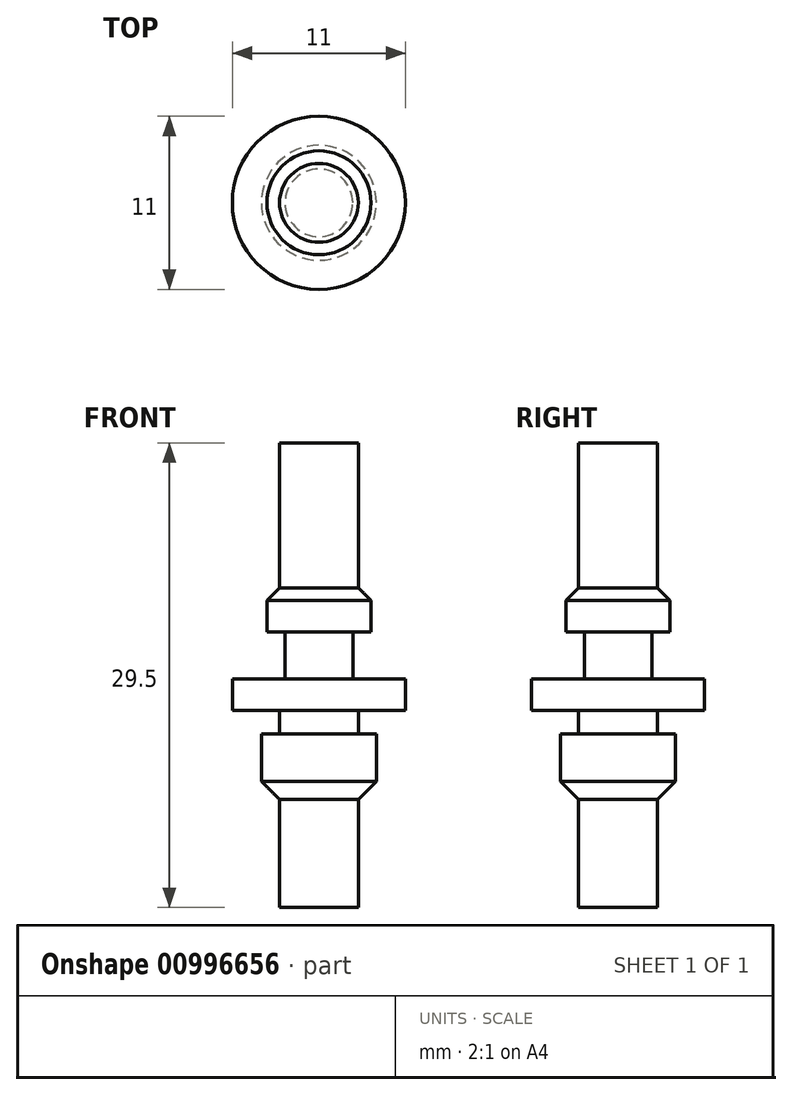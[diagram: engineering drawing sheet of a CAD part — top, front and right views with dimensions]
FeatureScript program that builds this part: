
annotation { "Feature Type Name" : "Feature", "Feature Type Description" : "" }
export const myFeature = defineFeature(function(context is Context, id is Id, definition is map)
    precondition{}
    {
        {
            var Q0;
            Q0=qCreatedBy(makeId("Top.planeOp"),FACE);
            var sketch = newSketch(context, id + "F0", { "sketchPlane" : qUnion([Q0])});
            skCircle(sketch, "E0", {"center": v(0, 0) * mm, "radius": 5.5 * mm});
            skSolve(sketch);
        }
        {
            var Q0;
            Q0=qSketchRegion(id+"F0",true);
            extrude(context, id + "F1", {"entities" : qUnion([Q0]), "depth" : 2 * mm, "offsetDistance" : 25 * mm});
        }
        {
            var Q0;
            Q0=makeQuery(id+"F1.opExtrude","CAP_FACE",FACE,{"disambiguationData":[OSD([sQuery(id+"F0.wireOp",EDGE,"E0")])],"isStart":false});
            var sketch = newSketch(context, id + "F2", { "sketchPlane" : qUnion([Q0])});
            skCircle(sketch, "E1", {"center": v(0, 0) * mm, "radius": 2.15 * mm});
            skSolve(sketch);
        }
        {
            var Q0;
            Q0=qSketchRegion(id+"F2",true);
            extrude(context, id + "F3", {"entities" : qUnion([Q0]), "operationType" : NewBodyOperationType.ADD, "depth" : 3 * mm, "offsetDistance" : 25 * mm});
        }
        {
            var Q0;
            Q0=makeQuery(id+"F3.opExtrude","CAP_FACE",FACE,{"disambiguationData":[OSD([sQuery(id+"F2.wireOp",EDGE,"E1")])],"isStart":false});
            var sketch = newSketch(context, id + "F4", { "sketchPlane" : qUnion([Q0])});
            skCircle(sketch, "E2", {"center": v(0, 0) * mm, "radius": 3.3 * mm});
            skSolve(sketch);
        }
        {
            var Q0;
            Q0=qSketchRegion(id+"F4",true);
            extrude(context, id + "F5", {"entities" : qUnion([Q0]), "operationType" : NewBodyOperationType.ADD, "depth" : 12 * mm, "offsetDistance" : 25 * mm});
        }
        {
            var Q0;
            Q0=makeQuery(id+"F5.opExtrude","CAP_FACE",FACE,{"disambiguationData":[OSD([sQuery(id+"F4.wireOp",EDGE,"E2")])],"isStart":false});
            var sketch = newSketch(context, id + "F6", { "sketchPlane" : qUnion([Q0])});
            skCircle(sketch, "E3", {"center": v(0, 0) * mm, "radius": 2.5 * mm});
            skCircle(sketch, "E4", {"center": v(0, 0) * mm, "radius": 5 * mm});
            skSolve(sketch);
        }
        {
            var Q0;
            Q0=qSketchRegion(id+"F6",true);
            extrude(context, id + "F7", {"entities" : qUnion([Q0]), "operationType" : NewBodyOperationType.REMOVE, "oppositeDirection" : true, "depth" : 7 * mm, "offsetDistance" : 25 * mm});
        }
        {
            var Q0;
            Q0=makeQuery(id+"F7.boolean.opBoolean","INTERSECT",EDGE,{"derivedFrom":[makeQuery(id+"F5.opExtrude","SWEPT_FACE",FACE,{"disambiguationData":[OSD([sQuery(id+"F4.wireOp",EDGE,"E2")])]}),makeQuery(id+"F7.opExtrude","CAP_FACE",FACE,{"disambiguationData":[OSD([sQuery(id+"F6.wireOp",EDGE,"E3"),sQuery(id+"F6.wireOp",EDGE,"E4")])],"isStart":false})]});
            chamfer(context, id + "F8", {"entities" : qUnion([Q0]), "width" : 3 * mm, "tangentPropagation" : true});
        }
        {
            var Q0;
            Q0=makeQuery(id+"F1.opExtrude","CAP_FACE",FACE,{"disambiguationData":[OSD([sQuery(id+"F0.wireOp",EDGE,"E0")])],"isStart":true});
            var sketch = newSketch(context, id + "F9", { "sketchPlane" : qUnion([Q0])});
            skCircle(sketch, "E5", {"center": v(0, 0) * mm, "radius": 2.5 * mm});
            skSolve(sketch);
        }
        {
            var Q0;
            Q0=qSketchRegion(id+"F9",true);
            extrude(context, id + "F10", {"entities" : qUnion([Q0]), "operationType" : NewBodyOperationType.ADD, "depth" : 1.5 * mm, "offsetDistance" : 25 * mm});
        }
        {
            var Q0;
            Q0=makeQuery(id+"F10.opExtrude","CAP_FACE",FACE,{"disambiguationData":[OSD([sQuery(id+"F9.wireOp",EDGE,"E5")])],"isStart":false});
            var sketch = newSketch(context, id + "F11", { "sketchPlane" : qUnion([Q0])});
            skCircle(sketch, "E6", {"center": v(0, 0) * mm, "radius": 3.65 * mm});
            skSolve(sketch);
        }
        {
            var Q0;
            Q0=qSketchRegion(id+"F11",true);
            extrude(context, id + "F12", {"entities" : qUnion([Q0]), "operationType" : NewBodyOperationType.ADD, "depth" : 11 * mm, "offsetDistance" : 25 * mm});
        }
        {
            var Q0;
            Q0=makeQuery(id+"F12.opExtrude","CAP_FACE",FACE,{"disambiguationData":[OSD([sQuery(id+"F11.wireOp",EDGE,"E6")])],"isStart":false});
            var sketch = newSketch(context, id + "F13", { "sketchPlane" : qUnion([Q0])});
            skCircle(sketch, "E7", {"center": v(0, 0) * mm, "radius": 2.5 * mm});
            skCircle(sketch, "E8", {"center": v(0, 0) * mm, "radius": 5 * mm});
            skSolve(sketch);
        }
        {
            var Q0;
            Q0=qSketchRegion(id+"F13",true);
            extrude(context, id + "F14", {"entities" : qUnion([Q0]), "operationType" : NewBodyOperationType.REMOVE, "oppositeDirection" : true, "depth" : 5 * mm, "offsetDistance" : 25 * mm});
        }
        {
            var Q0;
            Q0=makeQuery(id+"F14.boolean.opBoolean","INTERSECT",EDGE,{"derivedFrom":[makeQuery(id+"F12.opExtrude","SWEPT_FACE",FACE,{"disambiguationData":[OSD([sQuery(id+"F11.wireOp",EDGE,"E6")])]}),makeQuery(id+"F14.opExtrude","CAP_FACE",FACE,{"disambiguationData":[OSD([sQuery(id+"F13.wireOp",EDGE,"E7"),sQuery(id+"F13.wireOp",EDGE,"E8")])],"isStart":false})]});
            chamfer(context, id + "F15", {"entities" : qUnion([Q0]), "width" : 3 * mm, "tangentPropagation" : true});
        }
    });
